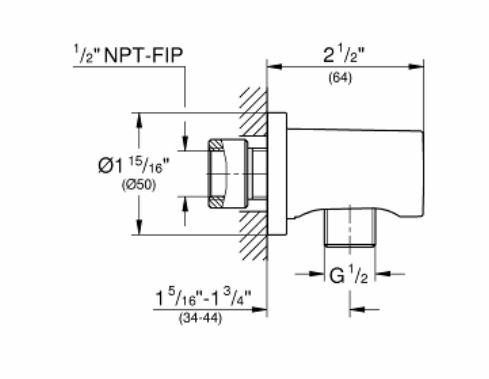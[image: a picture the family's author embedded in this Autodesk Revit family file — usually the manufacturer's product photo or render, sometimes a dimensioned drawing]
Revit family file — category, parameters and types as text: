
# Revit family: Commercial_Rainshower_System-GROHE-Cosmopolitan-29429 _Series
name_source: partatom
category: Plumbing Fixtures
units: mm (PartAtom-declared; Revit-internal decimal feet)

## family parameters
Cut with Voids When Loaded = No
Host = Face
OmniClass Number = 23.45.05.14.17
OmniClass Title = Showers
Part Type = Normal
Room Calculation Point = No
Round Connector Dimension = Use Diameter
Shared = Yes

## types (2) — shared parameters
24 043- Tempesta® Cosmopolitan 100 showerhead, 4 sprays, 1.75gpm = Yes
26 046- Tempesta® Cosmopolitan 100 handshower, 2 sprays, 1.75gpm = Yes
26 635- Rainshower™ wall union = Yes
27 412- Relexa® 6 ¼” shower arm = Yes
27 521- Tempesta® Cosmopolitan 24” Shower Bar = Yes
28 417- RotaFlex Metal Longlife metallic hose = Yes
29 434- Cosmopolitan Pressure Balance Valve Trim with 2-Way Diverter = Yes
35 117- GrohSafe™ 3.0 Pressure Balance Rough Valve with Integrated Diverter = Yes
ASME A112.18.1/CSA B125.1/ASSE 1016 = Yes
ASSE 1016 = Yes
Assembly Code = D2010710
CEC Compliant = Yes
CW Connection = Yes
CWFU = 3
CalGreen Compliant = Yes
Cold Water Connection Diameter = 1/2"
Connection Diameter = 1/2"
Default Elevation = 0"
Description = COSMOPOLITAN- Pressure Balance Rainshower Set
Double check valves = Included
EPA WaterSense® Certified = Yes
Flow Rate = Max. 1.75gpm (6.6L/min)
HW Connection = Yes
HWFU = 3
Height- Diverter = 48"
Height- Showerhead = 78"
Hot Water Connection Diameter = 1/2"
IAPMO Compliance = Massachusetts Plumbing Board Approved, Energy Policy Act of 1992, CSA B125.16
Installation Type = Wall Mounted
Manufacturer = GROHE
Price = Prices may vary. Please consult Manufacturer Representative for most up-to-date price list.
Tempered Water Connection = Yes
URL = https://www.grohe.us
Vent Connection = No
WFU = 4
Waste Connection = No

## per-type parameters (varying)
| type | Finish | Material |
| 29429000 | Metal-Grohe-000-StarLight Chrome | Metal-Grohe-000-StarLight Chrome |
| 29429EN0 | Metal-Grohe-EN0-Brushed Nickel Infinity Finish | Metal-Grohe-EN0-Brushed Nickel Infinity Finish |

note: column(s) folded — value = type name in every type: Model

## geometry (parser evidence)
native form markers: Sweep x21
no freeform markers — native parametric forms only
